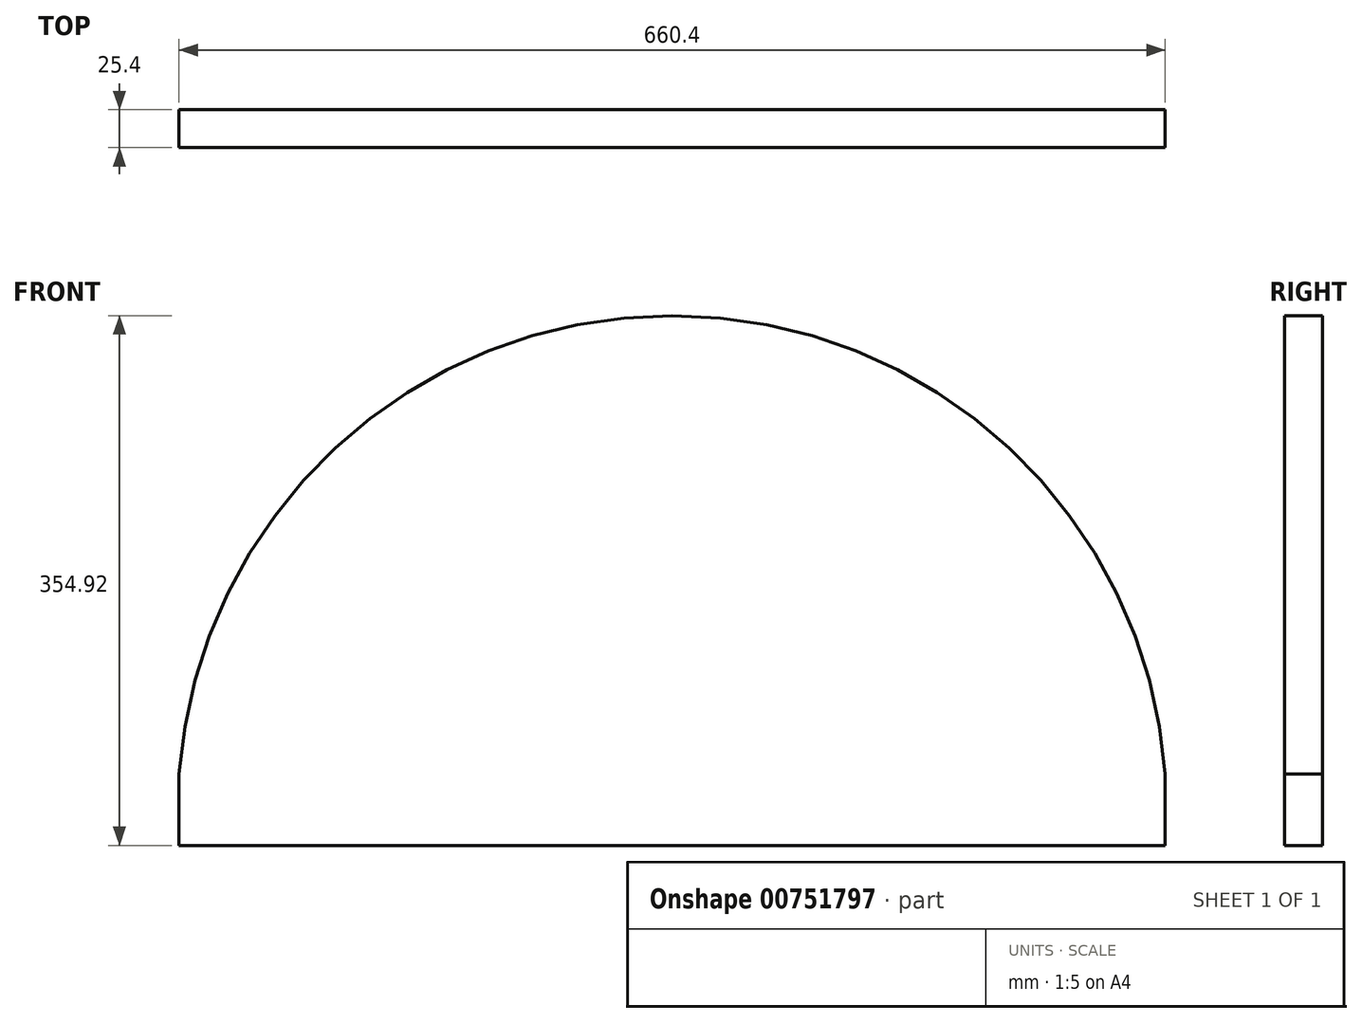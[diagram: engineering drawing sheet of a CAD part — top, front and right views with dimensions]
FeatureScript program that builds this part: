
annotation { "Feature Type Name" : "Feature", "Feature Type Description" : "" }
export const myFeature = defineFeature(function(context is Context, id is Id, definition is map)
    precondition{}
    {
        {
            var Q0;
            Q0=qCreatedBy(makeId("Front.planeOp"),FACE);
            var sketch = newSketch(context, id + "F0", { "sketchPlane" : qUnion([Q0])});
            skLineSegment(sketch, "E0.bottom", {"start": v(330.2, 177.8) * mm, "end": v(-330.2, 177.8) * mm});
            skLineSegment(sketch, "E0.top", {"start": v(330.2, -177.8) * mm, "end": v(-330.2, -177.8) * mm});
            skLineSegment(sketch, "E0.left", {"start": v(330.2, 177.8) * mm, "end": v(330.2, -177.8) * mm});
            skLineSegment(sketch, "E0.right", {"start": v(-330.2, 177.8) * mm, "end": v(-330.2, -177.8) * mm});
            skPoint(sketch, "E0.middle", {"position": v(0, 0) * mm});
            skArc(sketch, "E1", {"start": v(330.2, -177.8) * mm, "mid": v(0, 177.12) * mm, "end": v(-330.2, -177.8) * mm});
            skSolve(sketch);
        }
        {
            var Q0;
            {var subQ0=sQuery(id+"F0.wireOp",EDGE,"E0.top");Q0=makeQuery(id+"F0.imprint","IMPRINT",FACE,{"disambiguationData":[TD([[makeQuery(id+"F0.imprint","IMPRINT",EDGE,{"derivedFrom":subQ0}),-1.0]])]});}
            extrude(context, id + "F1", {"entities" : qUnion([Q0]), "depth" : 25.4 * mm, "offsetDistance" : 25.4 * mm});
        }
    });
